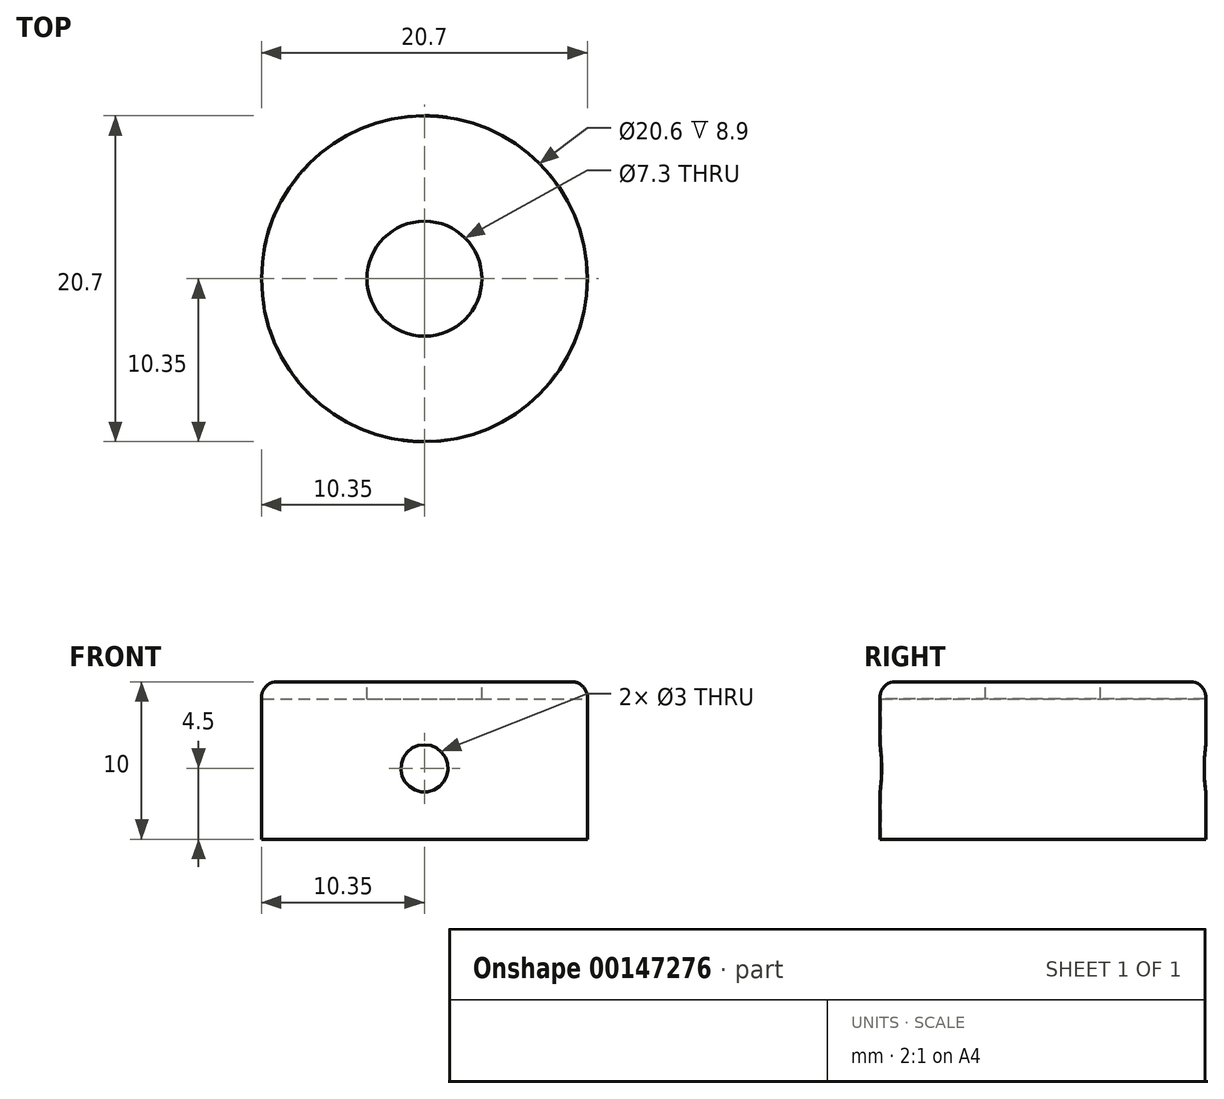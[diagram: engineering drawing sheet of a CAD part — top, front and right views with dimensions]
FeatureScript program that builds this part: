
annotation { "Feature Type Name" : "Feature", "Feature Type Description" : "" }
export const myFeature = defineFeature(function(context is Context, id is Id, definition is map)
    precondition{}
    {
        {
            var Q0;
            Q0=qCreatedBy(makeId("Top.planeOp"),FACE);
            var sketch = newSketch(context, id + "F0", { "sketchPlane" : qUnion([Q0])});
            skCircle(sketch, "E0", {"center": v(0, 0) * mm, "radius": 10.35 * mm});
            skSolve(sketch);
        }
        {
            var Q0;
            Q0 = qSketchRegion(id + "F0", true);
            extrude(context, id + "F1", {"entities" : qUnion([Q0]), "depth" : 10 * mm});
        }
        {
            var Q0;
            Q0=makeQuery(id+"F1.opExtrude","CAP_EDGE",EDGE,{"disambiguationData":[OSD([sQuery(id+"F0.wireOp",EDGE,"E0")])],"isStart":false});
            fillet(context, id + "F2", {"entities" : qUnion([Q0]), "radius" : 1 * mm, "tangentPropagation" : true, "allowEdgeOverflow" : false});
        }
        {
            var Q0;
            Q0=makeQuery(id+"F1.opExtrude","CAP_FACE",FACE,{"disambiguationData":[OSD([sQuery(id+"F0.wireOp",EDGE,"E0")])],"isStart":false});
            var sketch = newSketch(context, id + "F3", { "sketchPlane" : qUnion([Q0])});
            skCircle(sketch, "E1", {"center": v(0, 0) * mm, "radius": 3.65 * mm});
            skSolve(sketch);
        }
        {
            var Q0;
            Q0 = qSketchRegion(id + "F3", true);
            extrude(context, id + "F4", {"entities" : qUnion([Q0]), "operationType" : NewBodyOperationType.REMOVE, "oppositeDirection" : true, "depth" : 25 * mm});
        }
        {
            var Q0;
            Q0=makeQuery(id+"F1.opExtrude","CAP_FACE",FACE,{"disambiguationData":[OSD([sQuery(id+"F0.wireOp",EDGE,"E0")])],"isStart":true});
            var sketch = newSketch(context, id + "F5", { "sketchPlane" : qUnion([Q0])});
            skCircle(sketch, "E2", {"center": v(0, 0) * mm, "radius": 10.3 * mm});
            skSolve(sketch);
        }
        {
            var Q0;
            Q0 = qSketchRegion(id + "F5", true);
            var Q1;
            Q1=makeQuery(id+"F2.opFillet","BLEND_FACE",FACE,{"disambiguationData":[OSD([sQuery(id+"F0.wireOp",EDGE,"E0")])]});
            extrude(context, id + "F6", {"entities" : qUnion([Q0]), "operationType" : NewBodyOperationType.REMOVE, "oppositeDirection" : true, "endBoundEntityFace" : qUnion([Q1]), "depth" : 8.9 * mm});
        }
        {
            var Q0;
            Q0=qCreatedBy(makeId("Front.planeOp"),FACE);
            var sketch = newSketch(context, id + "F7", { "sketchPlane" : qUnion([Q0])});
            skLineSegment(sketch, "E3", {"start": v(0, 0) * mm, "end": v(0, 4.5) * mm});
            skCircle(sketch, "E4", {"center": v(0, 4.5) * mm, "radius": 1.5 * mm});
            skSolve(sketch);
        }
        {
            var Q0;
            Q0 = qSketchRegion(id + "F7", true);
            extrude(context, id + "F8", {"entities" : qUnion([Q0]), "operationType" : NewBodyOperationType.REMOVE, "endBound" : BoundingType.SYMMETRIC, "depth" : 25 * mm});
        }
    });
